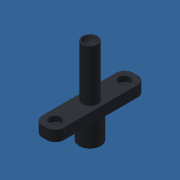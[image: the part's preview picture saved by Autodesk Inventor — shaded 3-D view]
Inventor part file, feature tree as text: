
AUTODESK INVENTOR PART (.ipt)
format: ipt  version: 2018.2 (Build 222227000, 227)  size: 292,352 bytes
history: native  units: in
note: dims shown in document units (in); Inventor stores cm internally (conversion verified against a paired STEP export)
features: sketch x4, hole x3, fillet x2, revolve x1, extrude x1
ambient origin geometry x8: Origin, YZ Plane, XZ Plane, XY Plane, X Axis, Y Axis, Z Axis, Center Point
bodies: Solid1 (feature_tree)
feature tree (11):
  revolve  "Revolution1"  [1 undecoded]
  sketch  "Sketch2"  dims[d2=0.4331in d3=0.625in]
  hole  "Hole1"  [1 undecoded]
  hole  "Hole2"  [1 undecoded]
  extrude  "Extrusion1"  Depth=0.016in
  hole  "Hole3"  [1 undecoded]
  fillet  "Fillet1"  Radius=2.0in
  fillet  "Fillet2"  Radius=0.25in
  sketch  "Sketch1"  dims[d0=0.3563in d1=0.0394in]
  sketch  "Sketch3"  dims[d4=1.0in d5=1.5in]
  sketch  "Sketch4"  dims[d6=90.0deg d7=0.05in d8=0.75in d9=0.375in d10=0.25in d11=0.5635in d12=1.0in d13=0.8108in d14=0.313in d15=0.273in d16=0.0246in d17=0.327in d18=0.375in d19=0.25in d20=0.5635in d21=0.6in d22=0.8108in d23=2.625in d24=0.32in d25=0.0in d26=2.0in d27=0.177in d28=0.273in d29=0.313in d30=0.164in d31=0.5635in d32=0.6in d33=0.8108in d34=0.25in d35=0.016in]
note: 4 required parameter values undecoded (feature->parameter linkage not recoverable at this tier; creation-order binding heuristic only, values carry confidence <= 0.55)